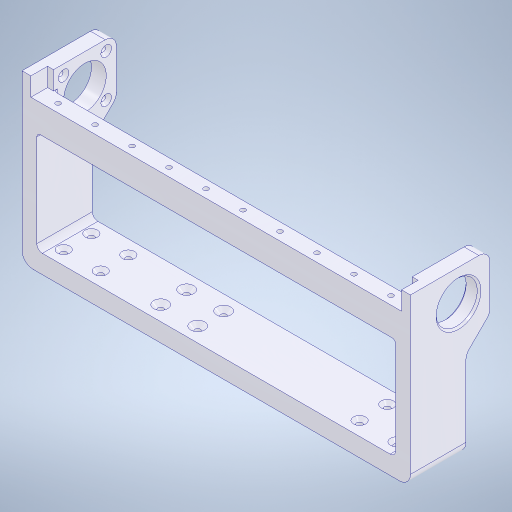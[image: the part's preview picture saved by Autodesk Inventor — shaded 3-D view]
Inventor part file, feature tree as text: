
AUTODESK INVENTOR PART (.ipt)
format: ipt  version: 2024.1 (Build 281209000, 209)  size: 464,896 bytes
history: native  units: in
note: dims shown in document units (in); Inventor stores cm internally (conversion verified against a paired STEP export)
features: extrude x10, sketch x10, chamfer x5, fillet x4
ambient origin geometry x8: Origin, YZ Plane, XZ Plane, XY Plane, X Axis, Y Axis, Z Axis, Center Point
bodies: Solid1 (feature_tree)
feature tree (29):
  extrude  "Extrusion1"  Depth=3.5433in
  extrude  "Extrusion2"  Depth=0.315in
  extrude  "Extrusion3"  Depth=0.3937in
  chamfer  "Chamfer1"  Distance=1.1811in
  extrude  "Extrusion9"  Depth=0.1181in
  chamfer  "Chamfer4"  Distance=0.2953in
  extrude  "Extrusion12"  Depth=0.0787in
  extrude  "Extrusion13"  Depth=0.0787in
  fillet  "Fillet3"  Radius=0.2953in
  extrude  "Extrusion14"  Depth=0.0787in
  extrude  "Extrusion15"  Depth=0.0787in
  chamfer  "Chamfer9"  Distance=0.2756in
  fillet  "Fillet4"  Radius=0.7874in
  fillet  "Fillet5"  Radius=0.7874in
  fillet  "Fillet6"  Radius=0.2756in
  extrude  "Extrusion17"  Depth=0.5906in
  chamfer  "Chamfer10"  Distance=0.5906in
  extrude  "Extrusion18"  Depth=0.5906in
  chamfer  "Chamfer11"  Distance=0.5906in
  sketch  "Sketch1"  dims[d0=8.2677in d1=3.5433in]
  sketch  "Sketch2"  dims[d2=1.1811in d3=0.0in d4=0.315in]
  sketch  "Sketch3"  dims[d5=0.315in d6=0.3937in d7=1.1811in d8=0.0in]
  sketch  "Sketch9"  dims[d9=0.1181in d10=0.1181in]
  sketch  "Sketch12"  dims[d11=0.1181in]
  sketch  "Sketch13"  dims[d12=0.1181in]
  sketch  "Sketch14"  dims[d13=0.1181in]
  sketch  "Sketch15"  dims[d14=0.1181in]
  sketch  "Sketch17"  dims[d15=0.1181in]
  sketch  "Sketch18"  dims[d16=0.1181in d18=0.2953in d19=0.2953in d20=0.2953in d21=0.2953in d22=0.7874in d23=0.7874in d24=0.2756in d25=0.7874in d26=0.7874in d27=0.2756in d28=0.5906in d29=0.5906in d30=0.5906in d31=0.5906in d33=5.5118in d34=5.5118in d35=1.1811in d36=0.0in d37=0.0709in d38=0.125in d39=45.0deg d74=1.1811in d75=1.1811in d76=0.5118in d77=0.0in d78=0.5118in d79=0.0787in d80=45.0deg d90=0.315in d97=0.3543in d98=0.5906in d99=0.3937in d100=7.6378in d101=0.0in d102=0.9055in d103=0.6693in d104=0.6693in d105=7.9528in d106=0.0in d107=0.0787in d108=0.3543in d109=0.126in d110=0.126in d111=0.3937in d112=0.0in d116=0.4016in d117=0.1772in d118=3.937in d120=0.7874in d121=0.3937in d123=0.3937in d125=0.5906in d126=0.0in d127=0.1024in d128=0.0984in d129=0.0984in d130=0.0984in d131=0.0984in d132=0.4528in d133=0.4528in d134=0.4528in d135=0.4528in d136=0.4528in d137=0.4528in d138=0.4528in d139=0.4528in d149=0.063in d150=0.0787in d151=45.0deg d152=0.1181in d153=0.2362in d154=0.2362in d155=0.1181in d156=0.1181in d157=0.1181in d158=0.1181in d159=0.315in d160=0.315in d161=0.315in d162=0.315in d163=0.7874in d164=0.7874in d165=2.3228in d166=2.3228in d167=0.3937in d168=0.0in d169=0.0906in d170=0.0787in d171=45.0deg d172=0.874in d173=0.0in d174=0.0in d175=0.0394in d176=0.0787in d177=45.0deg]
